# Revit family: Hager-WITTY PLUS ON PEDESTAL-pl-PL-PL
name_source: partatom
category: Electrical Fixtures
units: mm (PartAtom-declared; Revit-internal decimal feet)

## family parameters
Always vertical = Yes
Cut with Voids When Loaded = No
Maintain Annotation Orientation = No
Part Type = Normal
Room Calculation Point = No
Round Connector Dimension = Use Diameter
Shared = No
Work Plane-Based = No

## types (8) — shared parameters
BC_METADATA = {"ObjectGuid":"309c69a2-f6b5-4723-8d44-322179afe64e","ModelGuid":"04826155-e6fb-4358-826f-cf700e871803","VariantGuid":"d0dc6e8a-84e1-41b3-adf0-62c97217fd0d","Revision":"#2","VariantName":"REF 1"}
BC_MODEL_ID = 1528360
BC_OBJECT_ID = 511109
BC_OBJECT_VERSION = #1
Code hager = ADD_EC002883_ECVS_WO
EF000003 - Sposób montażu = Montaż ścienny
EF000008 - Szerokość = 250 mm  [stored 0.82021 ft]
EF000040 - Wysokość = 370 mm  [stored 1.21391 ft]
EF000049 - Głębokość = 150 mm
EF000458 - Z wyświetlaczem = No
EF001596 - Materiał obudowy = Tworzywo sztuczne
EF002136 - Moc znamionowa = 22000 W
EF003840 - Zakres napięcia wejściowego = 400 V
EF004293 - Odporność udarowa = IK10
EF005455 - Częstotliwość = 50/60 Hz
EF005474 - Stopień ochrony (IP) = IP55
EF007001 - Napięcie wyjściowe dla DC = 0 V
EF007353 - Maksymalny prąd wyjściowy dla DC = 0 A
EF009078 - Liczba punktów ładowania = 1
EF009089 - Z przyłączem = No
EF009300 - Maks. moc na punkt ładowania = 22000 W
EF009305 - Liczba gniazd ładowania typu 2 = 1
EF009313 - Z licznikiem energii = Yes
EF009314 - Z wyłącznikiem nadprądowym = No
EF009547 - LTE = No
EF011072 - Z obsługą IFTTT = No
EF012191 - Ze zintegrowanym czytnikiem kart RFID = Yes
EF012361 - NFC (Near Field Communication) = No
EF013154 - Praca w sieci przez WLAN = Yes
EF014925 - Kompatybilny z Apple HomeKit = No
EF014926 - Kompatybilny z Asystentem Google = No
EF014927 - Kompatybilny z Amazon Alexa = No
EF016385 - Standard komunikacji bezprzewodowej 5G = No
EF017508 - Możliwość pracy w sieci jako master = No
EF017509 - Wykrywanie prądu różnicowego DC = No
EF017510 - Wykrywanie zgrzania styków = No
EF017511 - Z przełącznikiem kluczykowym = No
EF017512 - Możliwość eksportu dzienników/logów ładowania = Yes
EF017513 - Wersja OpenChargePointProtocoll (OCPP) = 1.6
EF017515 - Podłącz i ładuj (ISO 15118) = No
EF017517 - Możliwość pracy w sieci jako jednostka rozszerzająca (extender) = No
EF017663 - Kabel ładowania zamykany na stałe w urządzeniu ładującym = No
EF017664 - Możliwość podłączenia do sieci poprzez LAN = Yes
EF017665 - Z licznikiem energii zgodnym z MID = Yes
EF017669 - Nadaje się do dynamicznego zarządzania obciążeniem = Yes
EF017672 - System backend w zestawie (monitorowanie i rozliczenia) = No
EF017972 - Obsługa i konfiguracja za pomocą aplikacji = Yes
EF025053 - Wykonanie przyłącza od strony instalacji = 3-fazowe
EFDE0066 - Zgodność z ustawą o pomiarach i wzorcowaniu (Eichrecht) = No
ETIM class code = EC002883
ETIM class name = Charging device E-Mobility
HG000003-Range = WITTY PLUS
HG000065-With socket TE = No
HG000099-Onfly Template ID = WittyOne_EVCS_On_Pedestal
Manufacturer = hager France
Name = WITTY PLUS ON PEDESTAL-PL
Name BIM&CO = Electricity
Name hager = ADD_ChargingStation_EC002883
Reference description = ECVS Witty 1x22kW 3P T2S
zero-valued in all types: Default Elevation, EF006577 - Liczba gniazd CEE (IEC 60309), EF008200 - Przekrój przewodu do podłączenia, EF009091 - Liczba wyłączników różnicowoprądowych typu A, EF009092 - Liczba wyłączników różnicowoprądowych typu B, EF009301 - Liczba złączy ładowania typu 1, EF009302 - Liczba złączy ładowania typu 1 CCS, EF009303 - Liczba złączy ładowania typu 2, EF009304 - Liczba złączy ładowania typu 2 CCS, EF009306 - Liczba złączy ładowania typu GB AC, EF009307 - Liczba złączy ładowania typu GB DC, EF009308 - Liczba gniazd ładowania typu GB, EF009309 - Liczba gniazd ładowania typu 3, EF009310 - Liczba złączy ładowania typu 2 CHAdeMO, EF009311 - Liczba domowych gniazdek elektrycznych

## per-type parameters (varying)
| type | BC_VARIANT_ID | EF014895 - Długość kabla ładowania | EF017668 - Zintegrowane zarządzanie obciążeniem statycznym | HG000004-Manufacturer reference |
| WITTY PLUS-1x22kW-3P-XVL122C-DOUBLE STATION-RECTANGULAR PEDESTAL | 1164418 | 6500 mm  [stored 21.3255 ft] | No | XVL122C / XVL122C / XVA135 |
| WITTY PLUS-1x22kW-3P-XVL122C-RECTANGULAR PEDESTAL | 1164423 | 6500 mm  [stored 21.3255 ft] | No | XVL122C / XVA130 |
| WITTY PLUS-1x22kW-3P-XVL122S-DOUBLE STATION-RECTANGULAR PEDESTAL | 1164424 | 0 mm  [stored 0 ft] | No | XVL122S / XVL122S / XVA135 |
| WITTY PLUS-1x22kW-3P-XVL122S-RECTANGULAR PEDESTAL | 1164425 | 0 mm  [stored 0 ft] | No | XVL122S / XVA130 |
| WITTY PLUS-1x22kW-3P-XVL122SFL-RECTANGULAR PEDESTAL | 1164426 | 0 mm  [stored 0 ft] | Yes | XVL122SFL / XVA130 |
| WITTY PLUS-1x22kW-3P-XVL122SFL-DOUBLE STATION-RECTANGULAR PEDESTAL | 1164427 | 0 mm  [stored 0 ft] | Yes | XVL122SFL / XVL122SFL / XVA135 |
| WITTY PLUS-1x22kW-3P-XVL122CFL-DOUBLE STATION-RECTANGULAR PEDESTAL | 1164428 | 6500 mm  [stored 21.3255 ft] | Yes | XVL122CFL / XVL122CFL / XVA135 |
| WITTY PLUS-1x22kW-3P-XVL122CFL-RECTANGULAR PEDESTAL | 1164429 | 6500 mm  [stored 21.3255 ft] | Yes | XVL122CFL / XVA130 |

note: column(s) folded — value = type name in every type: Reference

note: [stored X ft] marks values corroborated as IEEE doubles in the binary element streams (Revit-internal decimal feet)
